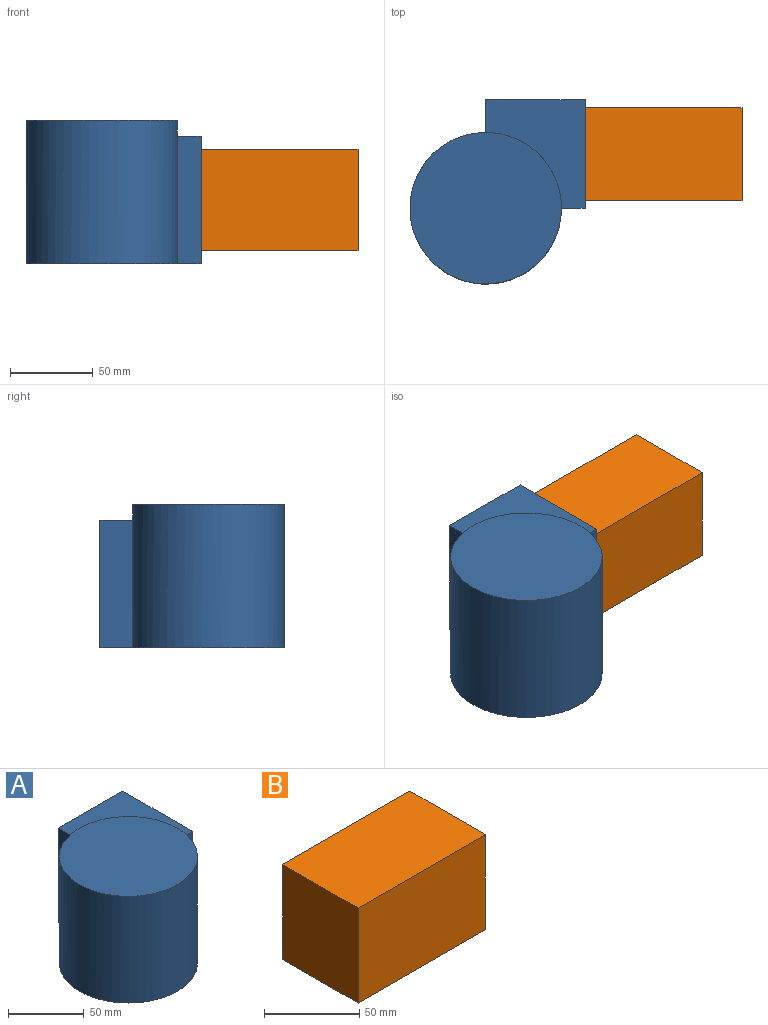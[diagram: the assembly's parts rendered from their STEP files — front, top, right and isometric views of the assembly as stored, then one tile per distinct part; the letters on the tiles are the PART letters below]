
ASSEMBLY  parts=2 mates=1
PART A: 8 faces, bbox 105.6x111x86.4 mm
  f0: cylinder r=45.7mm len=91.41mm, axis (0,0,-1), area 19291.2mm2, adj f1,f2,f3,f4,f5
  f1: plane 91.41x91.41mm, normal (0,0,1), area 6562.1mm2, adj f0
  f2: plane 111.04x105.65mm, normal (0,0,-1), area 8838.3mm2, adj f0,f3,f4,f6,f7
  f3: plane 76.72x14.24mm, normal (0,-1,0), area 1092.6mm2, adj f0,f2,f5,f7
  f4: plane 76.72x19.64mm, normal (-1,0,0), area 1506.5mm2, adj f0,f2,f5,f6
  f5: plane 65.34x59.94mm, normal (0,0,1), area 2276.1mm2, adj f0,f3,f4,f6,f7
  f6: plane 76.72x59.94mm, normal (0,1,0), area 4599.2mm2, adj f2,f4,f5,f7
  f7: plane 76.72x65.34mm, normal (1,0,0), area 5013.1mm2, adj f2,f3,f5,f6
PART B: 6 faces, bbox 94.6x56.1x61.1 mm
  f0: plane 94.64x56.13mm, normal (0,0,1), area 5312.3mm2, adj f1,f3,f4,f5
  f1: plane 61.06x56.13mm, normal (-1,0,0), area 3427.4mm2, adj f0,f2,f4,f5
  f2: plane 94.64x56.13mm, normal (0,0,-1), area 5312.3mm2, adj f1,f3,f4,f5
  f3: plane 61.06x56.13mm, normal (1,0,0), area 3427.4mm2, adj f0,f2,f4,f5
  f4: plane 94.64x61.06mm, normal (0,-1,0), area 5778.2mm2, adj f0,f1,f2,f3
  f5: plane 94.64x61.06mm, normal (0,1,0), area 5778.2mm2, adj f0,f1,f2,f3
PLACE A rot(axis=(0,0,1),0deg) t=(-97,-47.44,-26.86)mm
PLACE B t=(10.26,13.29,11.06)mm
MATE parallel A.f7 <-> B.f1  axis (1,0,0) through (-37.06,-14.77,11.5)mm
